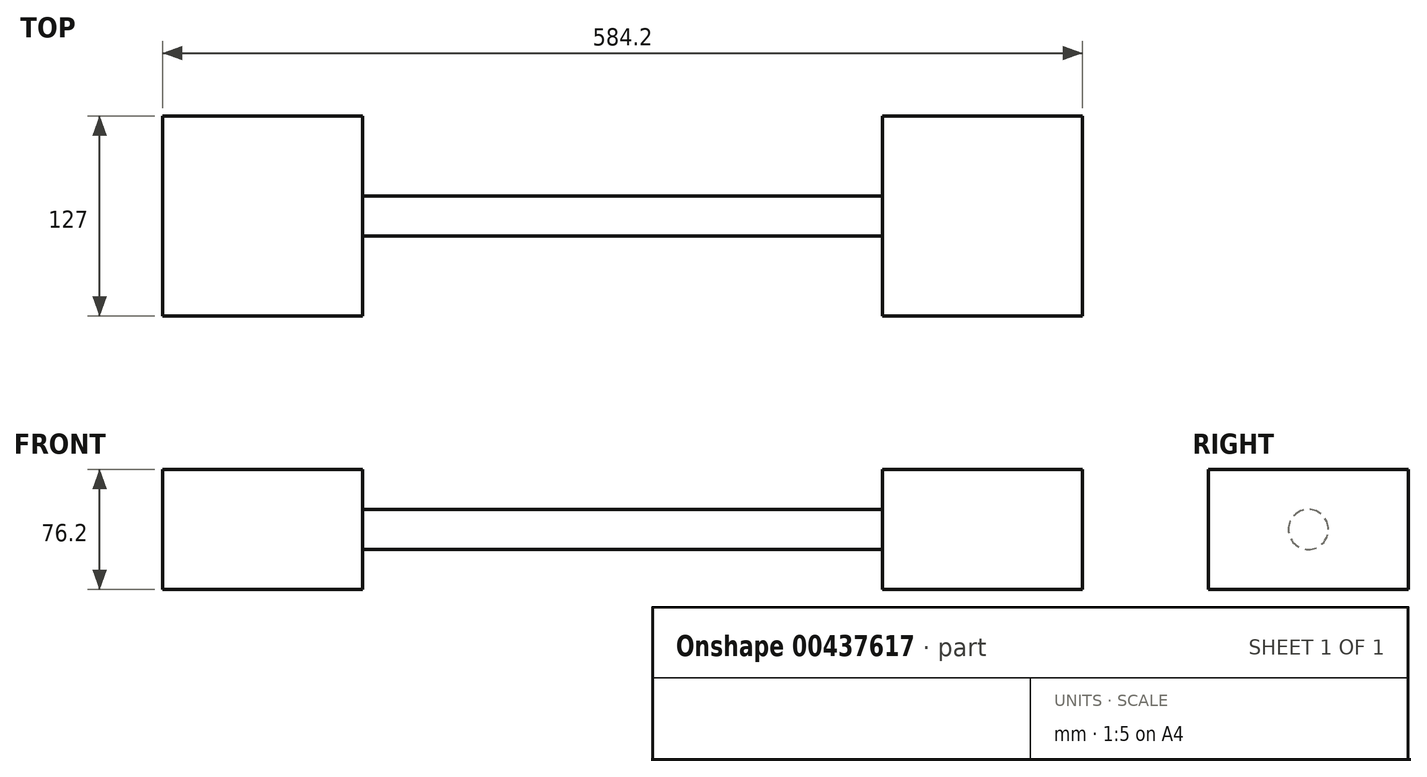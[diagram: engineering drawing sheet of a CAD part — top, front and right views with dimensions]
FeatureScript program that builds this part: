
annotation { "Feature Type Name" : "Feature", "Feature Type Description" : "" }
export const myFeature = defineFeature(function(context is Context, id is Id, definition is map)
    precondition{}
    {
        {
            var Q0;
            Q0=qCreatedBy(makeId("Top.planeOp"),FACE);
            var sketch = newSketch(context, id + "F0", { "sketchPlane" : qUnion([Q0])});
            skLineSegment(sketch, "E0.bottom", {"start": v(-79.67, -59.45) * mm, "end": v(47.33, -59.45) * mm});
            skLineSegment(sketch, "E0.top", {"start": v(-79.67, 67.55) * mm, "end": v(47.33, 67.55) * mm});
            skLineSegment(sketch, "E0.left", {"start": v(-79.67, -59.45) * mm, "end": v(-79.67, 67.55) * mm});
            skLineSegment(sketch, "E0.right", {"start": v(47.33, -59.45) * mm, "end": v(47.33, 67.55) * mm});
            skSolve(sketch);
        }
        {
            var Q0;
            Q0=makeQuery(id+"F0.imprint","IMPRINT",FACE,{"disambiguationData":[TD([[makeQuery(id+"F0.imprint","IMPRINT",EDGE,{"derivedFrom":sQuery(id+"F0.wireOp",EDGE,"E0.bottom")}),1.0]])]});
            extrude(context, id + "F1", {"entities" : qUnion([Q0]), "depth" : 76.2 * mm});
        }
        {
            var Q0;
            Q0=makeQuery(id+"F1.opExtrude","SWEPT_FACE",FACE,{"disambiguationData":[OSD([sQuery(id+"F0.wireOp",EDGE,"E0.right")])]});
            var sketch = newSketch(context, id + "F2", { "sketchPlane" : qUnion([Q0])});
            skLineSegment(sketch, "E1", {"start": v(-59.45, 38.1) * mm, "end": v(4.05, 38.1) * mm});
            skPoint(sketch, "E1.endSnap0", {"position": v(4.05, 76.2) * mm});
            skPoint(sketch, "E2.middle", {"position": v(4.05, 38.1) * mm});
            skPoint(sketch, "E2.left.end.orphan", {"position": v(10.4, 31.75) * mm});
            skPoint(sketch, "E2.bottom.start.orphan", {"position": v(13.03, 47.08) * mm});
            skPoint(sketch, "E3.orphan", {"position": v(-2.3, 44.45) * mm});
            skPoint(sketch, "E2.right.end.orphan", {"position": v(-4.93, 29.12) * mm});
            skCircle(sketch, "E4", {"center": v(4.05, 38.1) * mm, "radius": 12.7 * mm});
            skSolve(sketch);
        }
        {
            var Q0;
            Q0=qSketchRegion(id+"F2",true);
            extrude(context, id + "F3", {"entities" : qUnion([Q0]), "operationType" : NewBodyOperationType.ADD, "depth" : 330.2 * mm});
        }
        {
            var Q0;
            Q0=makeQuery(id+"F3.opExtrude","CAP_FACE",FACE,{"disambiguationData":[OSD([sQuery(id+"F2.wireOp",EDGE,"E4")])],"isStart":false});
            var sketch = newSketch(context, id + "F4", { "sketchPlane" : qUnion([Q0])});
            skLineSegment(sketch, "E5.bottom", {"start": v(67.55, 76.2) * mm, "end": v(-59.45, 76.2) * mm});
            skLineSegment(sketch, "E5.top", {"start": v(67.55, 0) * mm, "end": v(-59.45, 0) * mm});
            skLineSegment(sketch, "E5.left", {"start": v(67.55, 76.2) * mm, "end": v(67.55, 0) * mm});
            skLineSegment(sketch, "E5.right", {"start": v(-59.45, 76.2) * mm, "end": v(-59.45, 0) * mm});
            skPoint(sketch, "E5.middle", {"position": v(4.05, 38.1) * mm});
            skSolve(sketch);
        }
        {
            var Q0;
            Q0=makeQuery(id+"F4.imprint","IMPRINT",FACE,{"disambiguationData":[TD([[makeQuery(id+"F4.imprint","IMPRINT",EDGE,{"derivedFrom":sQuery(id+"F4.wireOp",EDGE,"E5.bottom")}),1.0]])]});
            var Q1;
            Q1=makeQuery(id+"F4.imprint","IMPRINT",FACE,{"disambiguationData":[TD([[makeQuery(id+"F4.imprint","IMPRINT",EDGE,{"derivedFrom":makeQuery(id+"F3.opExtrude","CAP_EDGE",EDGE,{"disambiguationData":[OSD([sQuery(id+"F2.wireOp",EDGE,"E4")])],"isStart":false})}),1.0]])]});
            extrude(context, id + "F5", {"entities" : qUnion([Q0, Q1]), "operationType" : NewBodyOperationType.ADD, "depth" : 127 * mm});
        }
    });
